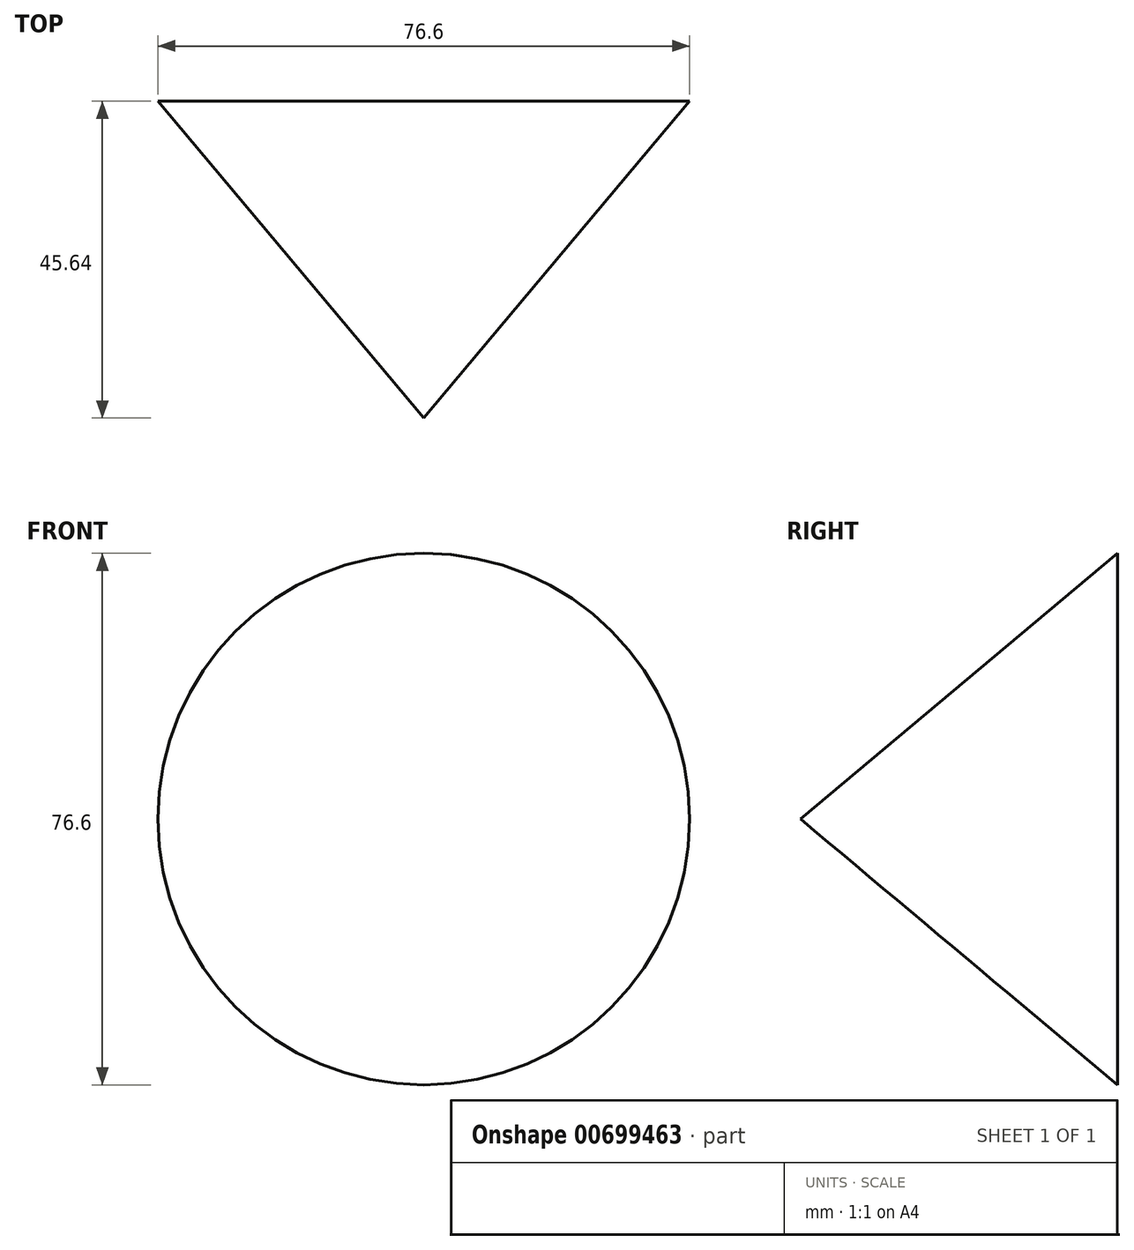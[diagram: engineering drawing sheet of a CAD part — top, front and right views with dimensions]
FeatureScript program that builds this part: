
annotation { "Feature Type Name" : "Feature", "Feature Type Description" : "" }
export const myFeature = defineFeature(function(context is Context, id is Id, definition is map)
    precondition{}
    {
        {
            var Q0;
            Q0=qCreatedBy(makeId("Front.planeOp"),FACE);
            var sketch = newSketch(context, id + "F0", { "sketchPlane" : qUnion([Q0])});
            skCircle(sketch, "E0", {"center": v(0, 0) * mm, "radius": 38.3 * mm});
            skSolve(sketch);
        }
        {
            var Q0;
            Q0=makeQuery(id+"F0.imprint","IMPRINT",FACE,{"disambiguationData":[TD([[makeQuery(id+"F0.imprint","IMPRINT",EDGE,{"derivedFrom":sQuery(id+"F0.wireOp",EDGE,"E0")}),1.0]])]});
            extrude(context, id + "F1", {"entities" : qUnion([Q0]), "depth" : 508 * mm, "offsetDistance" : 25.4 * mm, "hasDraft" : true, "draftAngle" : 40 * degree, "draftPullDirection" : true});
        }
    });
